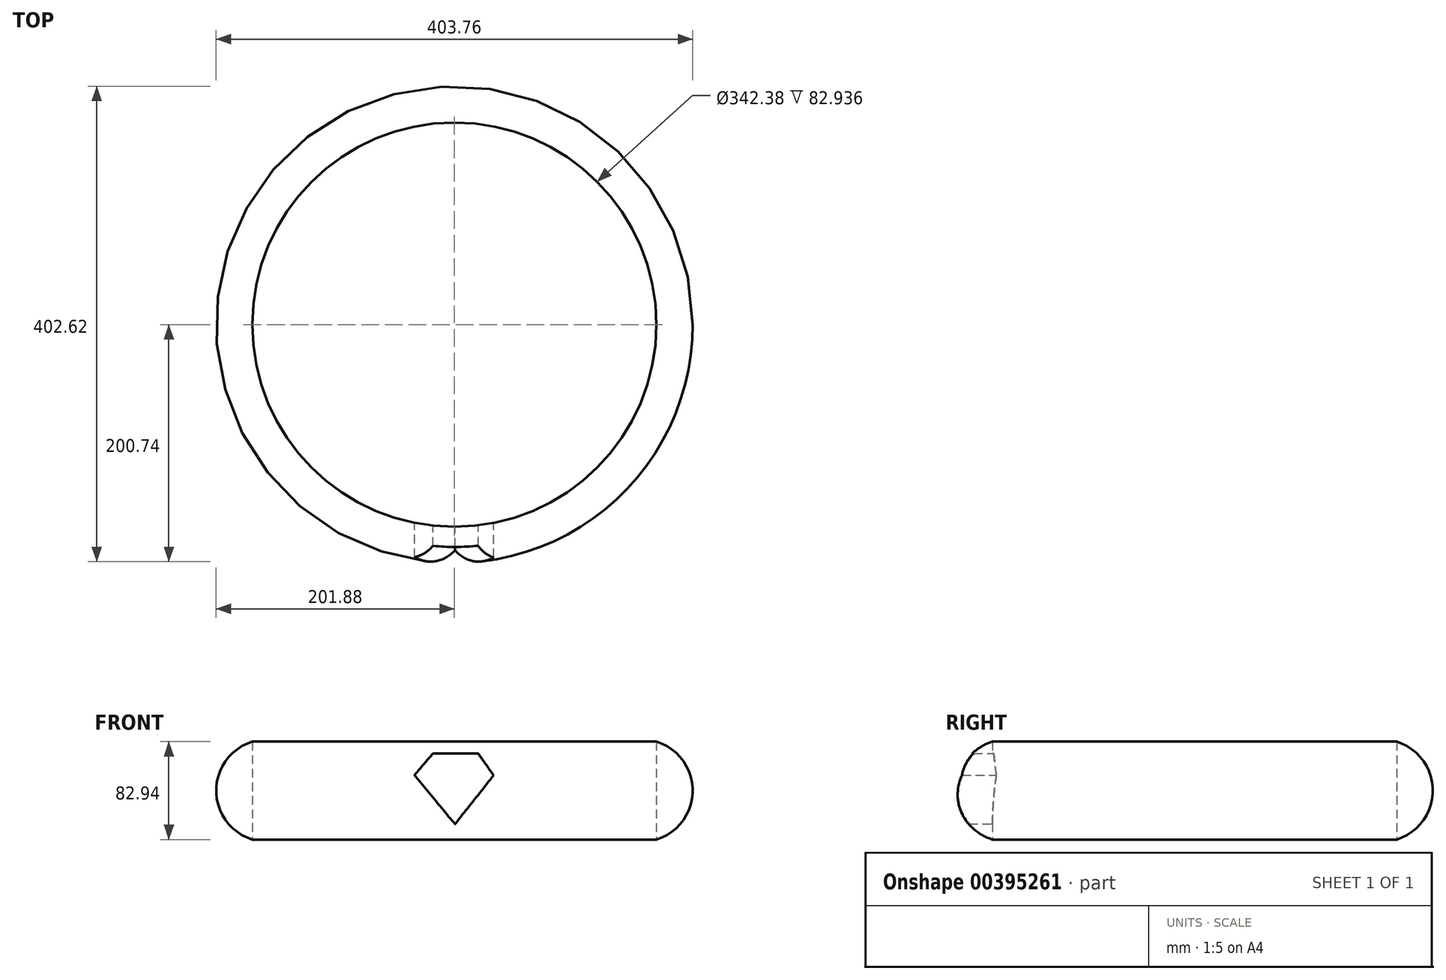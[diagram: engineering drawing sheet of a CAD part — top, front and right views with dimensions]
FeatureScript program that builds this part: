
annotation { "Feature Type Name" : "Feature", "Feature Type Description" : "" }
export const myFeature = defineFeature(function(context is Context, id is Id, definition is map)
    precondition{}
    {
        {
            var Q0;
            Q0=qCreatedBy(makeId("Top.planeOp"),FACE);
            var sketch = newSketch(context, id + "F0", { "sketchPlane" : qUnion([Q0])});
            skCircle(sketch, "E0", {"center": v(0, 0) * mm, "radius": 206.66 * mm});
            skSolve(sketch);
        }
        {
            var Q0;
            Q0=qCreatedBy(makeId("Right.planeOp"),FACE);
            var sketch = newSketch(context, id + "F1", { "sketchPlane" : qUnion([Q0])});
            skCircle(sketch, "E1", {"center": v(-158.53, 0) * mm, "radius": 43.36 * mm});
            skSolve(sketch);
        }
        {
            var Q0;
            Q0=makeQuery(id+"F1.imprint","IMPRINT",FACE,{"disambiguationData":[TD([[makeQuery(id+"F1.imprint","IMPRINT",EDGE,{"derivedFrom":sQuery(id+"F1.wireOp",EDGE,"E1")}),1.0]])]});
            var Q1;
            Q1=sQuery(id+"F0.wireOp",EDGE,"E0");
            sweep(context, id + "F2", {"profiles" : qUnion([Q0]), "path" : qUnion([Q1])});
        }
        {
            var Q0;
            Q0=qCreatedBy(makeId("Top.planeOp"),FACE);
            var sketch = newSketch(context, id + "F3", { "sketchPlane" : qUnion([Q0])});
            skCircle(sketch, "E2", {"center": v(0, 0) * mm, "radius": 171.19 * mm});
            skSolve(sketch);
        }
        {
            var Q0;
            Q0=qSketchRegion(id+"F3",true);
            extrude(context, id + "F4", {"entities" : qUnion([Q0]), "operationType" : NewBodyOperationType.REMOVE, "depth" : 439.93 * mm, "hasSecondDirection" : true, "secondDirectionOppositeDirection" : true, "secondDirectionDepth" : 259.08 * mm});
        }
        {
            var Q0;
            Q0=qCreatedBy(makeId("Top.planeOp"),FACE);
            var sketch = newSketch(context, id + "F5", { "sketchPlane" : qUnion([Q0])});
            skLineSegment(sketch, "E3", {"start": v(-284, -44.23) * mm, "end": v(-276.12, -35.04) * mm});
            skLineSegment(sketch, "E4", {"start": v(-276.12, -35.04) * mm, "end": v(-257.04, -35.04) * mm});
            skLineSegment(sketch, "E5", {"start": v(-257.04, -35.04) * mm, "end": v(-250.46, -44.36) * mm});
            skLineSegment(sketch, "E6", {"start": v(-250.46, -44.36) * mm, "end": v(-266.84, -65) * mm});
            skLineSegment(sketch, "E7", {"start": v(-266.84, -65) * mm, "end": v(-284, -44.23) * mm});
            skSolve(sketch);
        }
        {
            var Q0;
            Q0=qSketchRegion(id+"F5",true);
            extrude(context, id + "F6", {"entities" : qUnion([Q0]), "depth" : 91.44 * mm});
        }
        {
            var Q0;
            Q0=makeQuery(id+"F6.opExtrude","SWEPT_BODY",BODY,{"disambiguationData":[OSD([sQuery(id+"F5.wireOp",EDGE,"E3"),sQuery(id+"F5.wireOp",EDGE,"E4"),sQuery(id+"F5.wireOp",EDGE,"E5"),sQuery(id+"F5.wireOp",EDGE,"E6"),sQuery(id+"F5.wireOp",EDGE,"E7")])]});
            var Q1;
            Q1=makeQuery(id+"F6.opExtrude","CAP_EDGE",EDGE,{"disambiguationData":[OSD([sQuery(id+"F5.wireOp",EDGE,"E4")])],"isStart":false});
            transform(context, id + "F7", {"entities" : qUnion([Q0]), "transformType" : TransformType.ROTATION, "transformAxis" : qUnion([Q1]), "angle" : 90 * degree, "makeCopy" : false});
        }
        {
            var Q0;
            Q0=makeQuery(id+"F6.opExtrude","SWEPT_BODY",BODY,{"disambiguationData":[OSD([sQuery(id+"F5.wireOp",EDGE,"E3"),sQuery(id+"F5.wireOp",EDGE,"E4"),sQuery(id+"F5.wireOp",EDGE,"E5"),sQuery(id+"F5.wireOp",EDGE,"E6"),sQuery(id+"F5.wireOp",EDGE,"E7")])]});
            transform(context, id + "F8", {"entities" : qUnion([Q0]), "transformType" : TransformType.TRANSLATION_3D, "dx" : 273.3 * mm, "dy" : -174.5 * mm, "dz" : -10.67 * mm, "makeCopy" : false});
        }
        {
            var Q0;
            Q0=makeQuery(id+"F6.opExtrude","SWEPT_BODY",BODY,{"disambiguationData":[OSD([sQuery(id+"F5.wireOp",EDGE,"E3"),sQuery(id+"F5.wireOp",EDGE,"E4"),sQuery(id+"F5.wireOp",EDGE,"E5"),sQuery(id+"F5.wireOp",EDGE,"E6"),sQuery(id+"F5.wireOp",EDGE,"E7")])]});
            var Q1;
            Q1=qCreatedBy(makeId("Origin.pointOp"),VERTEX);
            transform(context, id + "F9", {"entities" : qUnion([Q0]), "transformType" : TransformType.SCALE_UNIFORMLY, "scale" : 2, "scalePoint" : qUnion([Q1]), "makeCopy" : false});
        }
        {
            var Q0;
            Q0=makeQuery(id+"F6.opExtrude","SWEPT_BODY",BODY,{"disambiguationData":[OSD([sQuery(id+"F5.wireOp",EDGE,"E3"),sQuery(id+"F5.wireOp",EDGE,"E4"),sQuery(id+"F5.wireOp",EDGE,"E5"),sQuery(id+"F5.wireOp",EDGE,"E6"),sQuery(id+"F5.wireOp",EDGE,"E7")])]});
            transform(context, id + "F10", {"entities" : qUnion([Q0]), "transformType" : TransformType.TRANSLATION_3D, "dx" : -12.45 * mm, "dy" : 129.03 * mm, "dz" : -130.05 * mm, "makeCopy" : false});
        }
        {
            var Q0;
            Q0=makeQuery(id+"F6.opExtrude","SWEPT_BODY",BODY,{"disambiguationData":[OSD([sQuery(id+"F5.wireOp",EDGE,"E3"),sQuery(id+"F5.wireOp",EDGE,"E4"),sQuery(id+"F5.wireOp",EDGE,"E5"),sQuery(id+"F5.wireOp",EDGE,"E6"),sQuery(id+"F5.wireOp",EDGE,"E7")])]});
            var Q1;
            Q1=makeQuery(id+"F2.opSweep","SWEPT_BODY",BODY,{"disambiguationData":[OSD([sQuery(id+"F0.wireOp",EDGE,"E0"),sQuery(id+"F1.wireOp",EDGE,"E1")])]});
            booleanBodies(context, id + "F11", {"operationType" : BooleanOperationType.SUBTRACTION, "tools" : qUnion([Q0]), "targets" : qUnion([Q1])});
        }
    });
